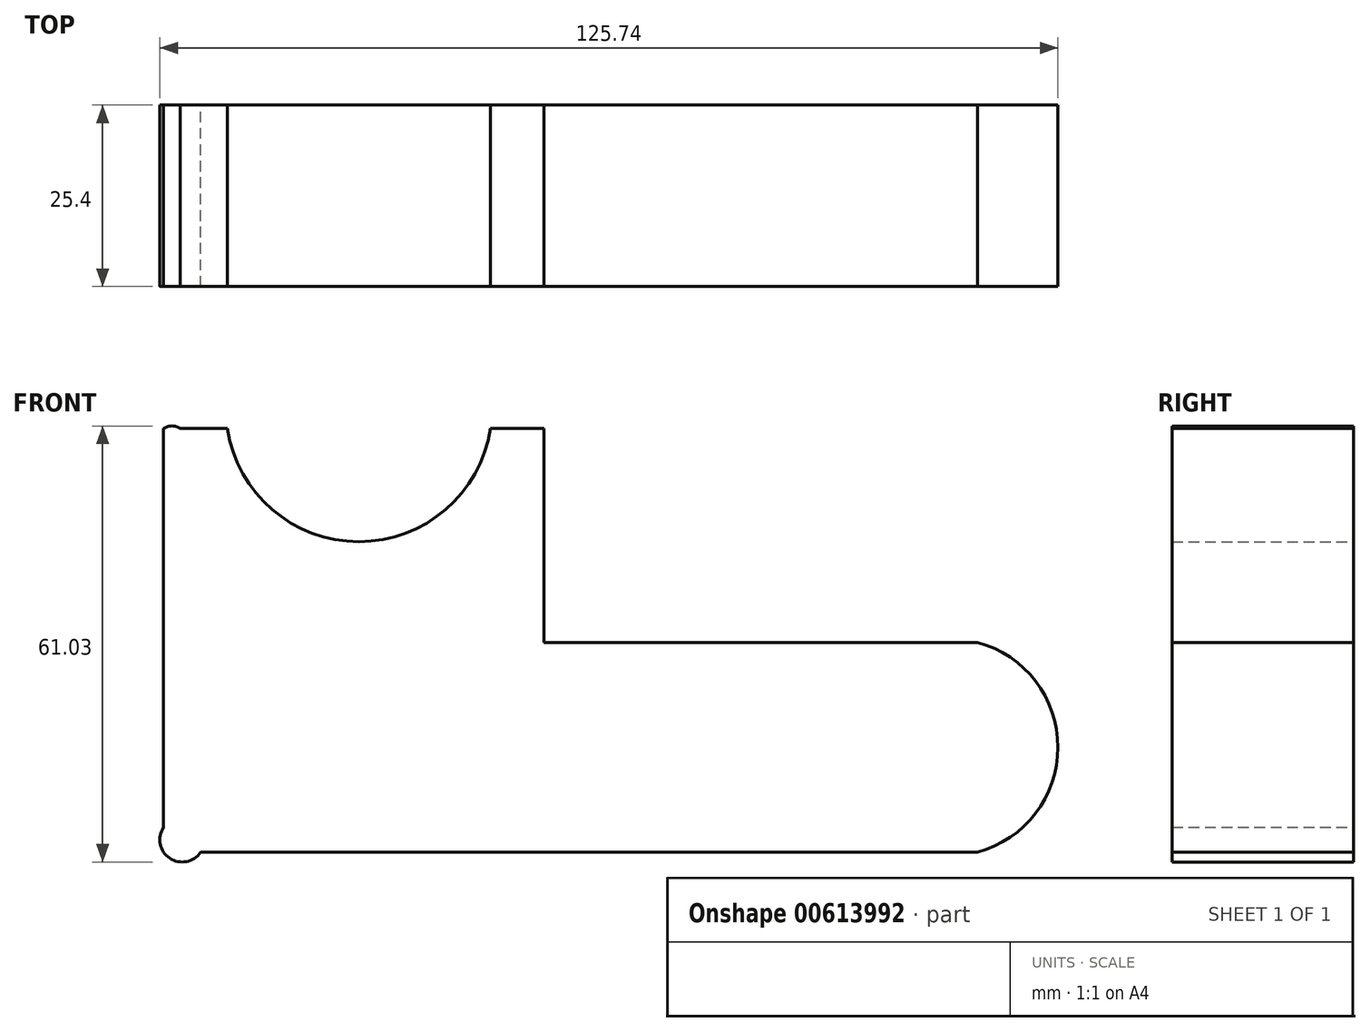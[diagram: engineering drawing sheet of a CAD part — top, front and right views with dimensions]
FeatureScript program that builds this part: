
annotation { "Feature Type Name" : "Feature", "Feature Type Description" : "" }
export const myFeature = defineFeature(function(context is Context, id is Id, definition is map)
    precondition{}
    {
        {
            var Q0;
            Q0=qCreatedBy(makeId("Front.planeOp"),FACE);
            var sketch = newSketch(context, id + "F0", { "sketchPlane" : qUnion([Q0])});
            skLineSegment(sketch, "E0", {"start": v(-65.19, -13.96) * mm, "end": v(-65.19, 45.33) * mm});
            skLineSegment(sketch, "E1", {"start": v(-65.19, 45.33) * mm, "end": v(-56.27, 45.33) * mm});
            skLineSegment(sketch, "E2", {"start": v(-19.43, 45.33) * mm, "end": v(-11.94, 45.33) * mm});
            skArc(sketch, "E3", {"start": v(-56.27, 45.33) * mm, "mid": v(-37.85, 29.5) * mm, "end": v(-19.43, 45.33) * mm});
            skLineSegment(sketch, "E4", {"start": v(-11.94, 45.33) * mm, "end": v(-11.94, 15.4) * mm});
            skLineSegment(sketch, "E5", {"start": v(-11.94, 15.4) * mm, "end": v(48.78, 15.4) * mm});
            skLineSegment(sketch, "E6", {"start": v(48.78, -13.96) * mm, "end": v(-63.17, -13.96) * mm});
            skArc(sketch, "E7", {"start": v(48.78, -13.96) * mm, "mid": v(60.03, 0.72) * mm, "end": v(48.78, 15.4) * mm});
            skArc(sketch, "E8", {"start": v(-65.19, -10.5) * mm, "mid": v(-64.32, -14.82) * mm, "end": v(-60, -13.96) * mm});
            skArc(sketch, "E9", {"start": v(-65.19, 41.88) * mm, "mid": v(-61.92, 43.6) * mm, "end": v(-65.19, 45.33) * mm});
            skSolve(sketch);
        }
        {
            var Q0;
            Q0 = qSketchRegion(id + "F0", true);
            extrude(context, id + "F1", {"entities" : qUnion([Q0]), "depth" : 25.4 * mm, "offsetDistance" : 25.4 * mm});
        }
    });
